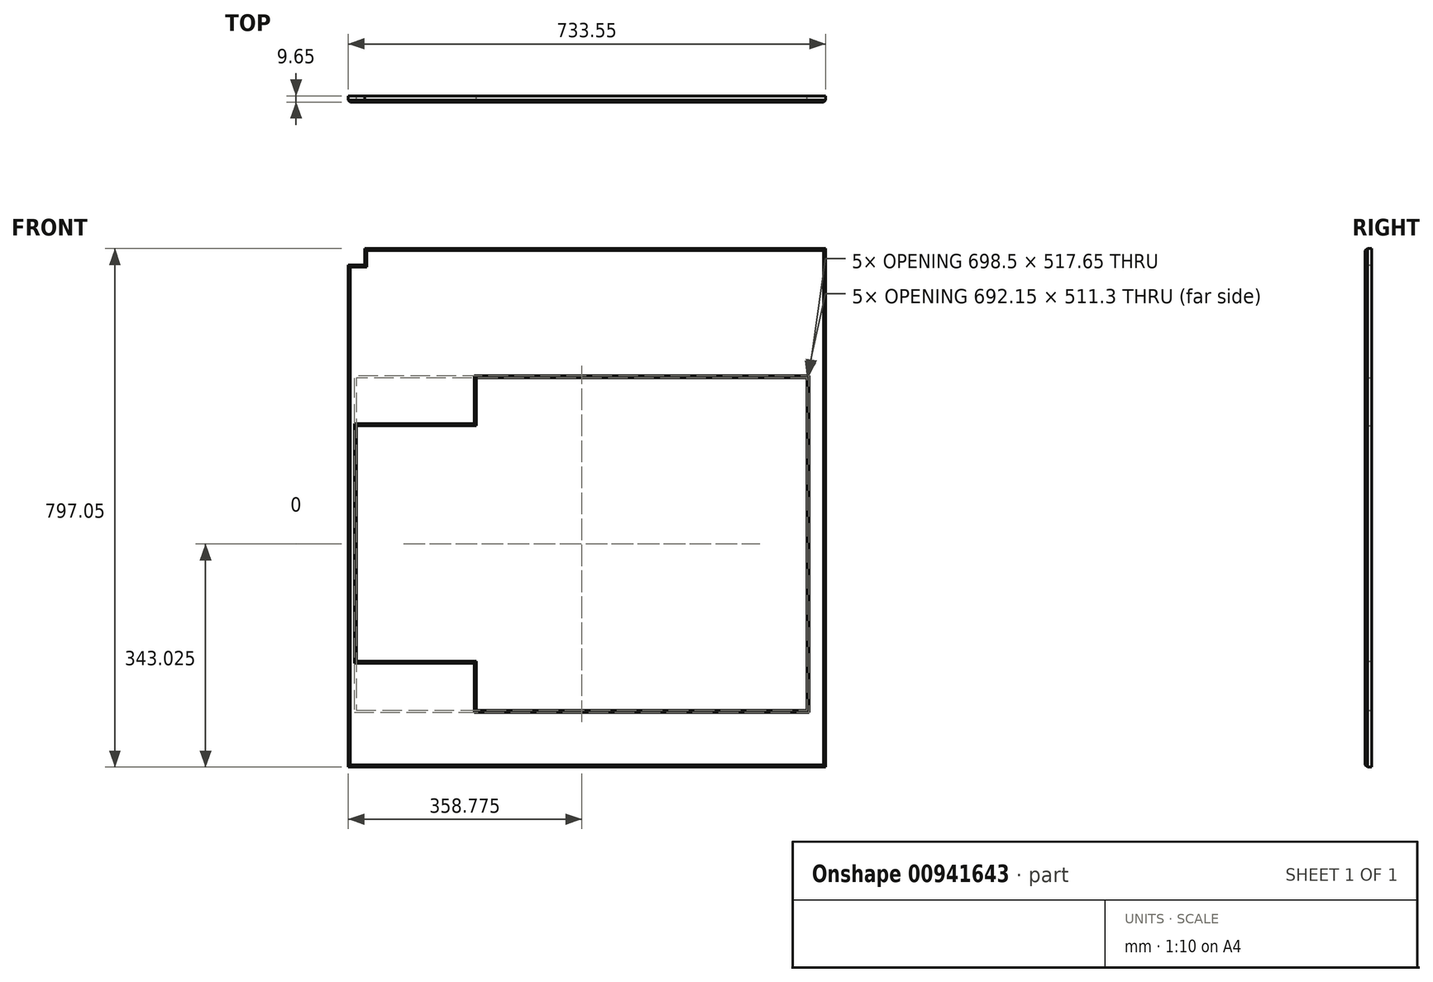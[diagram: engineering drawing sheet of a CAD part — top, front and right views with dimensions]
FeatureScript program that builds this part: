
annotation { "Feature Type Name" : "Feature", "Feature Type Description" : "" }
export const myFeature = defineFeature(function(context is Context, id is Id, definition is map)
    precondition{}
    {
        {
            var Q0;
            Q0=qCreatedBy(makeId("Front.planeOp"),FACE);
            var sketch = newSketch(context, id + "F0", { "sketchPlane" : qUnion([Q0])});
            skLineSegment(sketch, "E0.top", {"start": v(-447.8, -299.27) * mm, "end": v(285.75, -299.27) * mm});
            skLineSegment(sketch, "E0.right", {"start": v(285.75, 497.78) * mm, "end": v(285.75, -299.27) * mm});
            skLineSegment(sketch, "E1.right", {"start": v(-250.95, 299.4) * mm, "end": v(-250.95, 225.24) * mm});
            skLineSegment(sketch, "E2.right", {"start": v(-250.95, -136.71) * mm, "end": v(-250.95, -211.9) * mm});
            skLineSegment(sketch, "E3.bottom", {"start": v(-250.95, 299.4) * mm, "end": v(257.05, 299.4) * mm});
            skLineSegment(sketch, "E3.top", {"start": v(-250.95, -211.9) * mm, "end": v(257.05, -211.9) * mm});
            skLineSegment(sketch, "E3.right", {"start": v(257.05, 299.4) * mm, "end": v(257.05, -211.9) * mm});
            skLineSegment(sketch, "E4.top", {"start": v(-447.8, 472.38) * mm, "end": v(-422.4, 472.38) * mm});
            skLineSegment(sketch, "E4.right", {"start": v(-422.4, 497.78) * mm, "end": v(-422.4, 472.38) * mm});
            skLineSegment(sketch, "E5", {"start": v(-447.8, 472.38) * mm, "end": v(-447.8, -299.27) * mm});
            skLineSegment(sketch, "E6", {"start": v(-422.4, 497.78) * mm, "end": v(285.75, 497.78) * mm});
            skLineSegment(sketch, "E7.left", {"start": v(-435.1, 225.24) * mm, "end": v(-435.1, -136.71) * mm});
            skLineSegment(sketch, "E7.right", {"start": v(-250.95, 225.24) * mm, "end": v(-250.95, -136.71) * mm});
            skLineSegment(sketch, "E8", {"start": v(-435.1, 225.24) * mm, "end": v(-250.95, 225.24) * mm});
            skLineSegment(sketch, "E9", {"start": v(-435.1, -136.71) * mm, "end": v(-250.95, -136.71) * mm});
            skSolve(sketch);
        }
        {
            var Q0;
            Q0=makeQuery(id+"F0.imprint","IMPRINT",FACE,{"disambiguationData":[TD([[makeQuery(id+"F0.imprint","IMPRINT",EDGE,{"derivedFrom":sQuery(id+"F0.wireOp",EDGE,"E0.top")}),1.0]])]});
            extrude(context, id + "F1", {"entities" : qUnion([Q0]), "depth" : 9.65 * mm, "offsetDistance" : 25.4 * mm});
        }
        {
            var Q0;
            Q0=makeQuery(id+"F1.opExtrude","CAP_EDGE",EDGE,{"disambiguationData":[OSD([sQuery(id+"F0.wireOp",EDGE,"E6")])],"isStart":false});
            var Q1;
            Q1=makeQuery(id+"F1.opExtrude","CAP_FACE",FACE,{"disambiguationData":[OSD([sQuery(id+"F0.wireOp",EDGE,"E0.top"),sQuery(id+"F0.wireOp",EDGE,"E0.right"),sQuery(id+"F0.wireOp",EDGE,"E1.right"),sQuery(id+"F0.wireOp",EDGE,"E2.right"),sQuery(id+"F0.wireOp",EDGE,"E3.bottom"),sQuery(id+"F0.wireOp",EDGE,"E3.top"),sQuery(id+"F0.wireOp",EDGE,"E3.right"),sQuery(id+"F0.wireOp",EDGE,"E4.top"),sQuery(id+"F0.wireOp",EDGE,"E4.right"),sQuery(id+"F0.wireOp",EDGE,"E5"),sQuery(id+"F0.wireOp",EDGE,"E6"),sQuery(id+"F0.wireOp",EDGE,"E7.left"),sQuery(id+"F0.wireOp",EDGE,"E8"),sQuery(id+"F0.wireOp",EDGE,"E9")])],"isStart":false});
            chamfer(context, id + "F2", {"entities" : qUnion([Q0, Q1]), "width" : 3.17 * mm, "tangentPropagation" : true});
        }
    });
